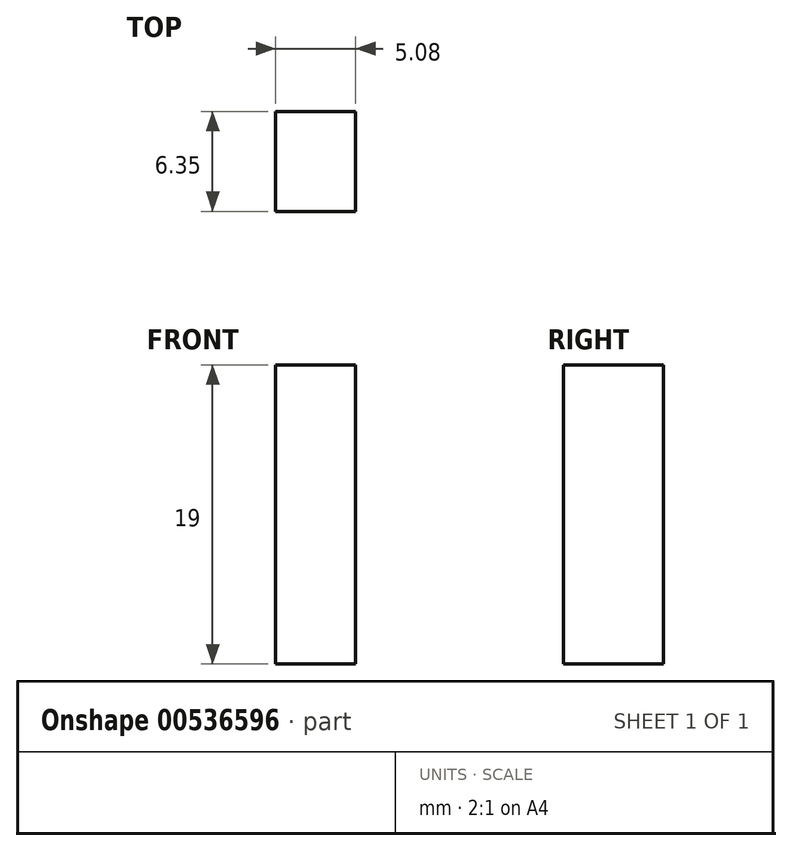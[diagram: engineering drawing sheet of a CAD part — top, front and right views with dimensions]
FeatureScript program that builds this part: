
annotation { "Feature Type Name" : "Feature", "Feature Type Description" : "" }
export const myFeature = defineFeature(function(context is Context, id is Id, definition is map)
    precondition{}
    {
        {
            var Q0;
            Q0=qCreatedBy(makeId("Front.planeOp"),FACE);
            var sketch = newSketch(context, id + "F0", { "sketchPlane" : qUnion([Q0])});
            skLineSegment(sketch, "E0.bottom", {"start": v(-50.85, 32.82) * mm, "end": v(-45.77, 32.82) * mm});
            skLineSegment(sketch, "E0.top", {"start": v(-50.85, 13.82) * mm, "end": v(-45.77, 13.82) * mm});
            skLineSegment(sketch, "E0.left", {"start": v(-50.85, 32.82) * mm, "end": v(-50.85, 13.82) * mm});
            skLineSegment(sketch, "E0.right", {"start": v(-45.77, 32.82) * mm, "end": v(-45.77, 13.82) * mm});
            skSolve(sketch);
        }
        {
            var Q0;
            Q0=makeQuery(id+"F0.imprint","IMPRINT",FACE,{"disambiguationData":[TD([[makeQuery(id+"F0.imprint","IMPRINT",EDGE,{"derivedFrom":sQuery(id+"F0.wireOp",EDGE,"E0.bottom")}),-1.0]])]});
            extrude(context, id + "F1", {"entities" : qUnion([Q0]), "depth" : 6.35 * mm, "offsetDistance" : 25.4 * mm});
        }
    });
